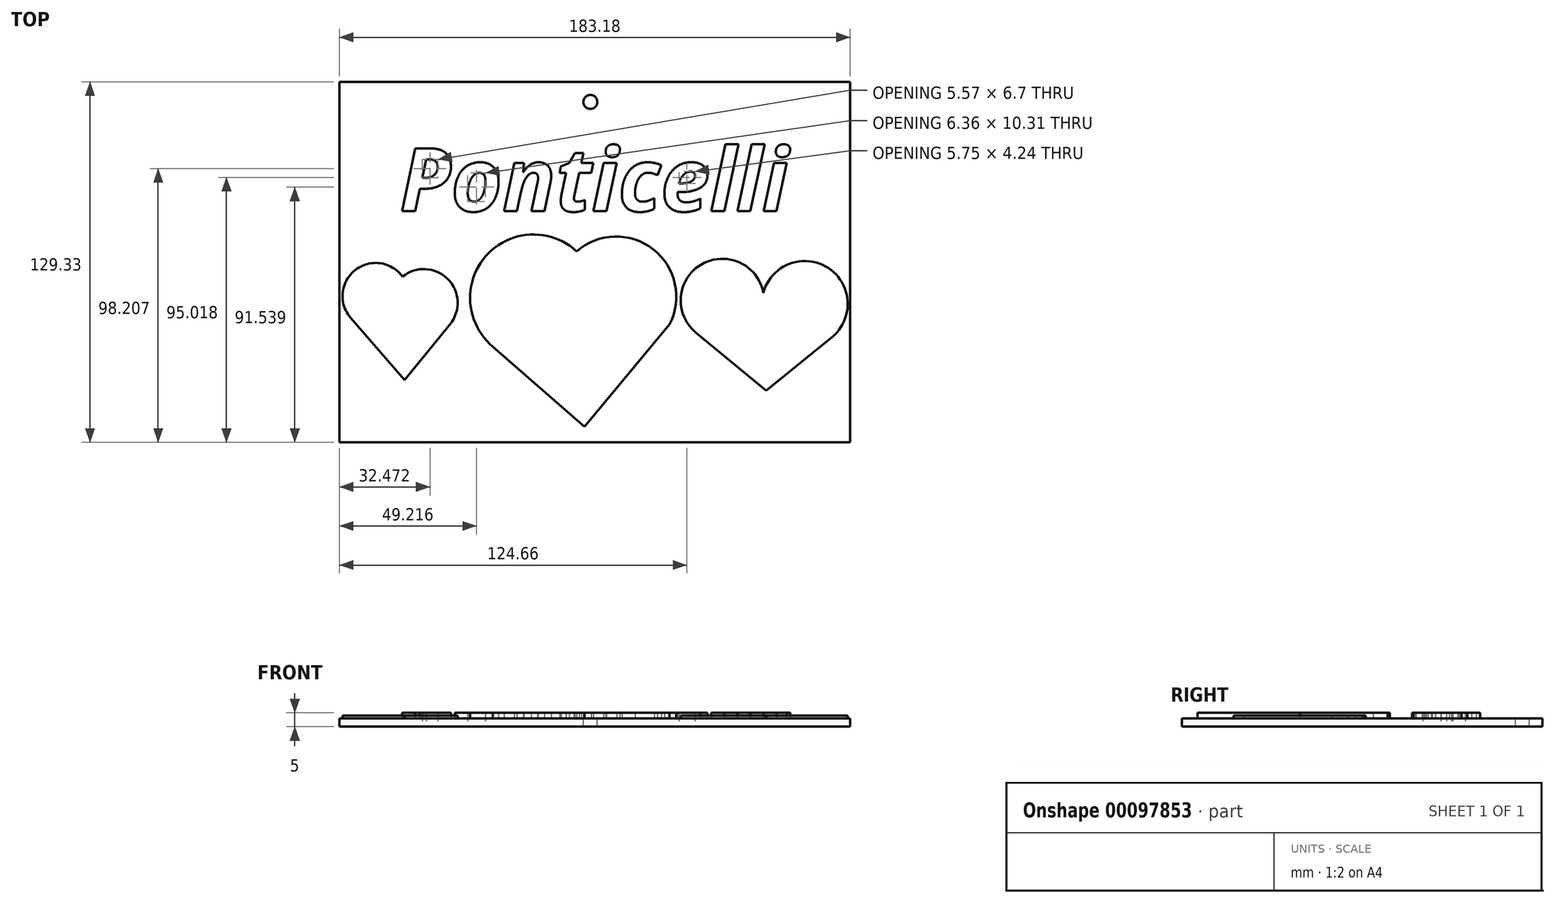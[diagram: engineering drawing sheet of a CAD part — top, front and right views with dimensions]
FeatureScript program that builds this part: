
annotation { "Feature Type Name" : "Feature", "Feature Type Description" : "" }
export const myFeature = defineFeature(function(context is Context, id is Id, definition is map)
    precondition{}
    {
        {
            var Q0;
            Q0=qCreatedBy(makeId("Top.planeOp"),FACE);
            var sketch = newSketch(context, id + "F0", { "sketchPlane" : qUnion([Q0])});
            skLineSegment(sketch, "E0.bottom", {"start": v(-99.25, 54.64) * mm, "end": v(83.93, 54.64) * mm});
            skLineSegment(sketch, "E0.top", {"start": v(-99.25, -74.7) * mm, "end": v(83.93, -74.7) * mm});
            skLineSegment(sketch, "E0.left", {"start": v(-99.25, 54.64) * mm, "end": v(-99.25, -74.7) * mm});
            skLineSegment(sketch, "E0.right", {"start": v(83.93, 54.64) * mm, "end": v(83.93, -74.7) * mm});
            skText(sketch, "E1", { "text": "Ponticelli", "fontName": "OpenSans-BoldItalic.ttf"});
            skArc(sketch, "E2", {"start": v(-14.18, -6.16) * mm, "mid": v(-46.73, -7.84) * mm, "end": v(-44.22, -40.34) * mm});
            skArc(sketch, "E3", {"start": v(19.14, -32.37) * mm, "mid": v(13.34, -5.46) * mm, "end": v(-14.18, -6.16) * mm});
            skLineSegment(sketch, "E4", {"start": v(-11.38, -69.06) * mm, "end": v(19.14, -32.37) * mm});
            skLineSegment(sketch, "E5", {"start": v(-11.38, -69.06) * mm, "end": v(-44.22, -40.34) * mm});
            const initialGuessF0  = {"E1": [-0.07762, 0.00822, 1, 0, 0.02276]};
            skSetInitialGuess(sketch, initialGuessF0);
            skSolve(sketch);
        }
        {
            var Q0;
            Q0=makeQuery(id+"F0.imprint","IMPRINT",FACE,{"disambiguationData":[TD([[makeQuery(id+"F0.imprint","IMPRINT",EDGE,{"derivedFrom":sQuery(id+"F0.wireOp",EDGE,"E1.sketch_text.stroke-0")}),-1.0]])]});
            var Q1;
            Q1=makeQuery(id+"F0.imprint","IMPRINT",FACE,{"disambiguationData":[TD([[makeQuery(id+"F0.imprint","IMPRINT",EDGE,{"derivedFrom":sQuery(id+"F0.wireOp",EDGE,"E1.sketch_text.stroke-15")}),-1.0]])]});
            var Q2;
            Q2=makeQuery(id+"F0.imprint","IMPRINT",FACE,{"disambiguationData":[TD([[makeQuery(id+"F0.imprint","IMPRINT",EDGE,{"derivedFrom":sQuery(id+"F0.wireOp",EDGE,"E1.sketch_text.stroke-33")}),-1.0]])]});
            var Q3;
            Q3=makeQuery(id+"F0.imprint","IMPRINT",FACE,{"disambiguationData":[TD([[makeQuery(id+"F0.imprint","IMPRINT",EDGE,{"derivedFrom":sQuery(id+"F0.wireOp",EDGE,"E1.sketch_text.stroke-50")}),-1.0]])]});
            var Q4;
            Q4=makeQuery(id+"F0.imprint","IMPRINT",FACE,{"disambiguationData":[TD([[makeQuery(id+"F0.imprint","IMPRINT",EDGE,{"derivedFrom":sQuery(id+"F0.wireOp",EDGE,"E1.sketch_text.stroke-69")}),-1.0]])]});
            var Q5;
            Q5=makeQuery(id+"F0.imprint","IMPRINT",FACE,{"disambiguationData":[TD([[makeQuery(id+"F0.imprint","IMPRINT",EDGE,{"derivedFrom":sQuery(id+"F0.wireOp",EDGE,"E1.sketch_text.stroke-76")}),-1.0]])]});
            var Q6;
            Q6=makeQuery(id+"F0.imprint","IMPRINT",FACE,{"disambiguationData":[TD([[makeQuery(id+"F0.imprint","IMPRINT",EDGE,{"derivedFrom":sQuery(id+"F0.wireOp",EDGE,"E1.sketch_text.stroke-80")}),-1.0]])]});
            var Q7;
            Q7=makeQuery(id+"F0.imprint","IMPRINT",FACE,{"disambiguationData":[TD([[makeQuery(id+"F0.imprint","IMPRINT",EDGE,{"derivedFrom":sQuery(id+"F0.wireOp",EDGE,"E1.sketch_text.stroke-98")}),-1.0]])]});
            var Q8;
            Q8=makeQuery(id+"F0.imprint","IMPRINT",FACE,{"disambiguationData":[TD([[makeQuery(id+"F0.imprint","IMPRINT",EDGE,{"derivedFrom":sQuery(id+"F0.wireOp",EDGE,"E1.sketch_text.stroke-122")}),-1.0]])]});
            var Q9;
            Q9=makeQuery(id+"F0.imprint","IMPRINT",FACE,{"disambiguationData":[TD([[makeQuery(id+"F0.imprint","IMPRINT",EDGE,{"derivedFrom":sQuery(id+"F0.wireOp",EDGE,"E1.sketch_text.stroke-126")}),-1.0]])]});
            var Q10;
            Q10=makeQuery(id+"F0.imprint","IMPRINT",FACE,{"disambiguationData":[TD([[makeQuery(id+"F0.imprint","IMPRINT",EDGE,{"derivedFrom":sQuery(id+"F0.wireOp",EDGE,"E1.sketch_text.stroke-130")}),-1.0]])]});
            var Q11;
            Q11=makeQuery(id+"F0.imprint","IMPRINT",FACE,{"disambiguationData":[TD([[makeQuery(id+"F0.imprint","IMPRINT",EDGE,{"derivedFrom":sQuery(id+"F0.wireOp",EDGE,"E1.sketch_text.stroke-137")}),-1.0]])]});
            var Q12;
            Q12=makeQuery(id+"F0.imprint","IMPRINT",FACE,{"disambiguationData":[TD([[makeQuery(id+"F0.imprint","IMPRINT",EDGE,{"derivedFrom":sQuery(id+"F0.wireOp",EDGE,"E2")}),1.0]])]});
            extrude(context, id + "F1", {"entities" : qUnion([Q0, Q1, Q2, Q3, Q4, Q5, Q6, Q7, Q8, Q9, Q10, Q11, Q12]), "depth" : 5 * mm});
        }
        {
            var Q0;
            Q0=makeQuery(id+"F0.imprint","IMPRINT",FACE,{"disambiguationData":[TD([[makeQuery(id+"F0.imprint","IMPRINT",EDGE,{"derivedFrom":sQuery(id+"F0.wireOp",EDGE,"E0.bottom")}),-1.0]])]});
            extrude(context, id + "F2", {"entities" : qUnion([Q0]), "operationType" : NewBodyOperationType.ADD, "depth" : 3 * mm});
        }
        {
            var Q0;
            Q0=makeQuery(id+"F2.opExtrude","CAP_FACE",FACE,{"disambiguationData":[OSD([sQuery(id+"F0.wireOp",EDGE,"E0.bottom"),sQuery(id+"F0.wireOp",EDGE,"E0.top"),sQuery(id+"F0.wireOp",EDGE,"E0.left"),sQuery(id+"F0.wireOp",EDGE,"E0.right"),sQuery(id+"F0.wireOp",EDGE,"E1.sketch_text.stroke-6"),sQuery(id+"F0.wireOp",EDGE,"E1.sketch_text.stroke-7"),sQuery(id+"F0.wireOp",EDGE,"E1.sketch_text.stroke-8"),sQuery(id+"F0.wireOp",EDGE,"E1.sketch_text.stroke-9"),sQuery(id+"F0.wireOp",EDGE,"E1.sketch_text.stroke-10"),sQuery(id+"F0.wireOp",EDGE,"E1.sketch_text.stroke-11"),sQuery(id+"F0.wireOp",EDGE,"E1.sketch_text.stroke-12"),sQuery(id+"F0.wireOp",EDGE,"E1.sketch_text.stroke-13"),sQuery(id+"F0.wireOp",EDGE,"E1.sketch_text.stroke-14"),sQuery(id+"F0.wireOp",EDGE,"E1.sketch_text.stroke-23"),sQuery(id+"F0.wireOp",EDGE,"E1.sketch_text.stroke-24"),sQuery(id+"F0.wireOp",EDGE,"E1.sketch_text.stroke-25"),sQuery(id+"F0.wireOp",EDGE,"E1.sketch_text.stroke-26"),sQuery(id+"F0.wireOp",EDGE,"E1.sketch_text.stroke-27"),sQuery(id+"F0.wireOp",EDGE,"E1.sketch_text.stroke-28"),sQuery(id+"F0.wireOp",EDGE,"E1.sketch_text.stroke-29"),sQuery(id+"F0.wireOp",EDGE,"E1.sketch_text.stroke-30"),sQuery(id+"F0.wireOp",EDGE,"E1.sketch_text.stroke-31"),sQuery(id+"F0.wireOp",EDGE,"E1.sketch_text.stroke-32"),sQuery(id+"F0.wireOp",EDGE,"E1.sketch_text.stroke-33"),sQuery(id+"F0.wireOp",EDGE,"E1.sketch_text.stroke-34"),sQuery(id+"F0.wireOp",EDGE,"E1.sketch_text.stroke-35"),sQuery(id+"F0.wireOp",EDGE,"E1.sketch_text.stroke-36"),sQuery(id+"F0.wireOp",EDGE,"E1.sketch_text.stroke-37"),sQuery(id+"F0.wireOp",EDGE,"E1.sketch_text.stroke-38"),sQuery(id+"F0.wireOp",EDGE,"E1.sketch_text.stroke-39"),sQuery(id+"F0.wireOp",EDGE,"E1.sketch_text.stroke-40"),sQuery(id+"F0.wireOp",EDGE,"E1.sketch_text.stroke-41"),sQuery(id+"F0.wireOp",EDGE,"E1.sketch_text.stroke-42"),sQuery(id+"F0.wireOp",EDGE,"E1.sketch_text.stroke-43"),sQuery(id+"F0.wireOp",EDGE,"E1.sketch_text.stroke-44"),sQuery(id+"F0.wireOp",EDGE,"E1.sketch_text.stroke-45"),sQuery(id+"F0.wireOp",EDGE,"E1.sketch_text.stroke-46"),sQuery(id+"F0.wireOp",EDGE,"E1.sketch_text.stroke-47"),sQuery(id+"F0.wireOp",EDGE,"E1.sketch_text.stroke-48"),sQuery(id+"F0.wireOp",EDGE,"E1.sketch_text.stroke-49"),sQuery(id+"F0.wireOp",EDGE,"E1.sketch_text.stroke-50"),sQuery(id+"F0.wireOp",EDGE,"E1.sketch_text.stroke-51"),sQuery(id+"F0.wireOp",EDGE,"E1.sketch_text.stroke-52"),sQuery(id+"F0.wireOp",EDGE,"E1.sketch_text.stroke-53"),sQuery(id+"F0.wireOp",EDGE,"E1.sketch_text.stroke-54"),sQuery(id+"F0.wireOp",EDGE,"E1.sketch_text.stroke-55"),sQuery(id+"F0.wireOp",EDGE,"E1.sketch_text.stroke-56"),sQuery(id+"F0.wireOp",EDGE,"E1.sketch_text.stroke-57"),sQuery(id+"F0.wireOp",EDGE,"E1.sketch_text.stroke-58"),sQuery(id+"F0.wireOp",EDGE,"E1.sketch_text.stroke-59"),sQuery(id+"F0.wireOp",EDGE,"E1.sketch_text.stroke-60"),sQuery(id+"F0.wireOp",EDGE,"E1.sketch_text.stroke-61"),sQuery(id+"F0.wireOp",EDGE,"E1.sketch_text.stroke-62"),sQuery(id+"F0.wireOp",EDGE,"E1.sketch_text.stroke-63"),sQuery(id+"F0.wireOp",EDGE,"E1.sketch_text.stroke-64"),sQuery(id+"F0.wireOp",EDGE,"E1.sketch_text.stroke-65"),sQuery(id+"F0.wireOp",EDGE,"E1.sketch_text.stroke-66"),sQuery(id+"F0.wireOp",EDGE,"E1.sketch_text.stroke-67"),sQuery(id+"F0.wireOp",EDGE,"E1.sketch_text.stroke-68"),sQuery(id+"F0.wireOp",EDGE,"E1.sketch_text.stroke-69"),sQuery(id+"F0.wireOp",EDGE,"E1.sketch_text.stroke-70"),sQuery(id+"F0.wireOp",EDGE,"E1.sketch_text.stroke-71"),sQuery(id+"F0.wireOp",EDGE,"E1.sketch_text.stroke-72"),sQuery(id+"F0.wireOp",EDGE,"E1.sketch_text.stroke-73"),sQuery(id+"F0.wireOp",EDGE,"E1.sketch_text.stroke-74"),sQuery(id+"F0.wireOp",EDGE,"E1.sketch_text.stroke-75"),sQuery(id+"F0.wireOp",EDGE,"E1.sketch_text.stroke-76"),sQuery(id+"F0.wireOp",EDGE,"E1.sketch_text.stroke-77"),sQuery(id+"F0.wireOp",EDGE,"E1.sketch_text.stroke-78"),sQuery(id+"F0.wireOp",EDGE,"E1.sketch_text.stroke-79"),sQuery(id+"F0.wireOp",EDGE,"E1.sketch_text.stroke-80"),sQuery(id+"F0.wireOp",EDGE,"E1.sketch_text.stroke-81"),sQuery(id+"F0.wireOp",EDGE,"E1.sketch_text.stroke-82"),sQuery(id+"F0.wireOp",EDGE,"E1.sketch_text.stroke-83"),sQuery(id+"F0.wireOp",EDGE,"E1.sketch_text.stroke-84"),sQuery(id+"F0.wireOp",EDGE,"E1.sketch_text.stroke-85"),sQuery(id+"F0.wireOp",EDGE,"E1.sketch_text.stroke-86"),sQuery(id+"F0.wireOp",EDGE,"E1.sketch_text.stroke-87"),sQuery(id+"F0.wireOp",EDGE,"E1.sketch_text.stroke-88"),sQuery(id+"F0.wireOp",EDGE,"E1.sketch_text.stroke-89"),sQuery(id+"F0.wireOp",EDGE,"E1.sketch_text.stroke-90"),sQuery(id+"F0.wireOp",EDGE,"E1.sketch_text.stroke-91"),sQuery(id+"F0.wireOp",EDGE,"E1.sketch_text.stroke-92"),sQuery(id+"F0.wireOp",EDGE,"E1.sketch_text.stroke-93"),sQuery(id+"F0.wireOp",EDGE,"E1.sketch_text.stroke-94"),sQuery(id+"F0.wireOp",EDGE,"E1.sketch_text.stroke-95"),sQuery(id+"F0.wireOp",EDGE,"E1.sketch_text.stroke-96"),sQuery(id+"F0.wireOp",EDGE,"E1.sketch_text.stroke-97"),sQuery(id+"F0.wireOp",EDGE,"E1.sketch_text.stroke-104"),sQuery(id+"F0.wireOp",EDGE,"E1.sketch_text.stroke-105"),sQuery(id+"F0.wireOp",EDGE,"E1.sketch_text.stroke-106"),sQuery(id+"F0.wireOp",EDGE,"E1.sketch_text.stroke-107"),sQuery(id+"F0.wireOp",EDGE,"E1.sketch_text.stroke-108"),sQuery(id+"F0.wireOp",EDGE,"E1.sketch_text.stroke-109"),sQuery(id+"F0.wireOp",EDGE,"E1.sketch_text.stroke-110"),sQuery(id+"F0.wireOp",EDGE,"E1.sketch_text.stroke-111"),sQuery(id+"F0.wireOp",EDGE,"E1.sketch_text.stroke-112"),sQuery(id+"F0.wireOp",EDGE,"E1.sketch_text.stroke-113"),sQuery(id+"F0.wireOp",EDGE,"E1.sketch_text.stroke-114"),sQuery(id+"F0.wireOp",EDGE,"E1.sketch_text.stroke-115"),sQuery(id+"F0.wireOp",EDGE,"E1.sketch_text.stroke-116"),sQuery(id+"F0.wireOp",EDGE,"E1.sketch_text.stroke-117"),sQuery(id+"F0.wireOp",EDGE,"E1.sketch_text.stroke-118"),sQuery(id+"F0.wireOp",EDGE,"E1.sketch_text.stroke-119"),sQuery(id+"F0.wireOp",EDGE,"E1.sketch_text.stroke-120"),sQuery(id+"F0.wireOp",EDGE,"E1.sketch_text.stroke-121"),sQuery(id+"F0.wireOp",EDGE,"E1.sketch_text.stroke-122"),sQuery(id+"F0.wireOp",EDGE,"E1.sketch_text.stroke-123"),sQuery(id+"F0.wireOp",EDGE,"E1.sketch_text.stroke-124"),sQuery(id+"F0.wireOp",EDGE,"E1.sketch_text.stroke-125"),sQuery(id+"F0.wireOp",EDGE,"E1.sketch_text.stroke-126"),sQuery(id+"F0.wireOp",EDGE,"E1.sketch_text.stroke-127"),sQuery(id+"F0.wireOp",EDGE,"E1.sketch_text.stroke-128"),sQuery(id+"F0.wireOp",EDGE,"E1.sketch_text.stroke-129"),sQuery(id+"F0.wireOp",EDGE,"E1.sketch_text.stroke-130"),sQuery(id+"F0.wireOp",EDGE,"E1.sketch_text.stroke-131"),sQuery(id+"F0.wireOp",EDGE,"E1.sketch_text.stroke-132"),sQuery(id+"F0.wireOp",EDGE,"E1.sketch_text.stroke-133"),sQuery(id+"F0.wireOp",EDGE,"E1.sketch_text.stroke-134"),sQuery(id+"F0.wireOp",EDGE,"E1.sketch_text.stroke-135"),sQuery(id+"F0.wireOp",EDGE,"E1.sketch_text.stroke-136"),sQuery(id+"F0.wireOp",EDGE,"E1.sketch_text.stroke-137"),sQuery(id+"F0.wireOp",EDGE,"E1.sketch_text.stroke-138"),sQuery(id+"F0.wireOp",EDGE,"E1.sketch_text.stroke-139"),sQuery(id+"F0.wireOp",EDGE,"E1.sketch_text.stroke-140"),sQuery(id+"F0.wireOp",EDGE,"E2"),sQuery(id+"F0.wireOp",EDGE,"E3"),sQuery(id+"F0.wireOp",EDGE,"E4"),sQuery(id+"F0.wireOp",EDGE,"E5")])],"isStart":false});
            var sketch = newSketch(context, id + "F3", { "sketchPlane" : qUnion([Q0])});
            skArc(sketch, "E6", {"start": v(-76.6, -15.25) * mm, "mid": v(-93.63, -12.9) * mm, "end": v(-95.22, -30.03) * mm});
            skArc(sketch, "E7", {"start": v(-59.54, -32.29) * mm, "mid": v(-60.37, -16.07) * mm, "end": v(-76.6, -15.25) * mm});
            skLineSegment(sketch, "E8", {"start": v(-75.85, -52.35) * mm, "end": v(-59.54, -32.29) * mm});
            skLineSegment(sketch, "E9", {"start": v(-59.54, -32.29) * mm, "end": v(-75.85, -52.35) * mm});
            skLineSegment(sketch, "E10", {"start": v(-75.85, -52.35) * mm, "end": v(-95.22, -30.03) * mm});
            skArc(sketch, "E11", {"start": v(77.38, -36.95) * mm, "mid": v(76, -12.1) * mm, "end": v(52.77, -21.03) * mm});
            skArc(sketch, "E12", {"start": v(52.77, -21.03) * mm, "mid": v(30.5, -10.88) * mm, "end": v(28.56, -35.28) * mm});
            skLineSegment(sketch, "E13", {"start": v(53.83, -56.17) * mm, "end": v(77.38, -36.95) * mm});
            skLineSegment(sketch, "E14", {"start": v(77.38, -36.95) * mm, "end": v(53.83, -56.17) * mm});
            skLineSegment(sketch, "E15", {"start": v(53.83, -56.17) * mm, "end": v(28.56, -35.28) * mm});
            skPoint(sketch, "E16", {"position": v(-9.24, 47.43) * mm});
            skCircle(sketch, "E17", {"center": v(-9.24, 47.43) * mm, "radius": 2.05 * mm});
            skSolve(sketch);
        }
        {
            var Q0;
            Q0=makeQuery(id+"F3.imprint","IMPRINT",FACE,{"disambiguationData":[TD([[makeQuery(id+"F3.imprint","IMPRINT",EDGE,{"derivedFrom":sQuery(id+"F3.wireOp",EDGE,"E6")}),1.0]])]});
            var Q1;
            Q1=makeQuery(id+"F3.imprint","IMPRINT",FACE,{"disambiguationData":[TD([[makeQuery(id+"F3.imprint","IMPRINT",EDGE,{"derivedFrom":sQuery(id+"F3.wireOp",EDGE,"E11")}),1.0]])]});
            extrude(context, id + "F4", {"entities" : qUnion([Q0, Q1]), "operationType" : NewBodyOperationType.ADD, "depth" : 1 * mm});
        }
        {
            var Q0;
            Q0=sQuery(id+"F3.wireOp",VERTEX,"E16");
            var Q1;
            Q1=makeQuery(id+"F1.opExtrude","SWEPT_BODY",BODY,{"disambiguationData":[OSD([sQuery(id+"F0.wireOp",EDGE,"E1.sketch_text.stroke-0"),sQuery(id+"F0.wireOp",EDGE,"E1.sketch_text.stroke-1"),sQuery(id+"F0.wireOp",EDGE,"E1.sketch_text.stroke-2"),sQuery(id+"F0.wireOp",EDGE,"E1.sketch_text.stroke-3"),sQuery(id+"F0.wireOp",EDGE,"E1.sketch_text.stroke-4"),sQuery(id+"F0.wireOp",EDGE,"E1.sketch_text.stroke-5"),sQuery(id+"F0.wireOp",EDGE,"E1.sketch_text.stroke-6"),sQuery(id+"F0.wireOp",EDGE,"E1.sketch_text.stroke-7"),sQuery(id+"F0.wireOp",EDGE,"E1.sketch_text.stroke-8"),sQuery(id+"F0.wireOp",EDGE,"E1.sketch_text.stroke-9"),sQuery(id+"F0.wireOp",EDGE,"E1.sketch_text.stroke-10"),sQuery(id+"F0.wireOp",EDGE,"E1.sketch_text.stroke-11"),sQuery(id+"F0.wireOp",EDGE,"E1.sketch_text.stroke-12"),sQuery(id+"F0.wireOp",EDGE,"E1.sketch_text.stroke-13"),sQuery(id+"F0.wireOp",EDGE,"E1.sketch_text.stroke-14")])]});
            hole(context, id + "F5", {"style" : HoleStyle.SIMPLE, "endStyle" : HoleEndStyle.THROUGH, "holeDiameter" : 5 * mm, "locations" : qUnion([Q0]), "scope" : qUnion([Q1]), "isTappedThrough" : true});
        }
    });
